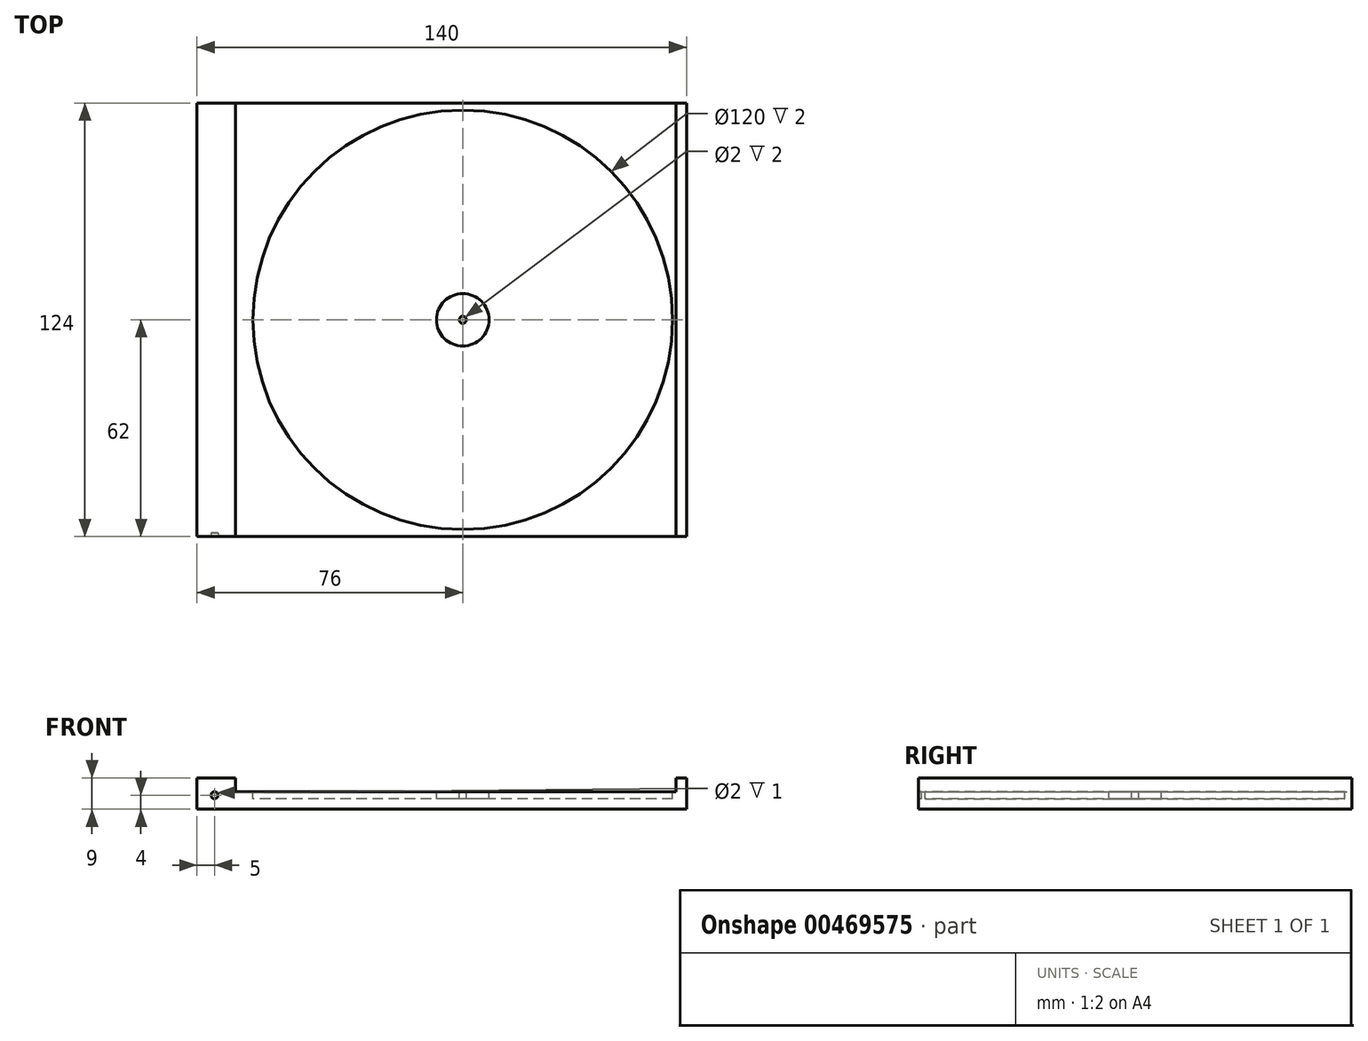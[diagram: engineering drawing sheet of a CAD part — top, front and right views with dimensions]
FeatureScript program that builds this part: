
annotation { "Feature Type Name" : "Feature", "Feature Type Description" : "" }
export const myFeature = defineFeature(function(context is Context, id is Id, definition is map)
    precondition{}
    {
        {
            var Q0;
            Q0=qCreatedBy(makeId("Top.planeOp"),FACE);
            var sketch = newSketch(context, id + "F0", { "sketchPlane" : qUnion([Q0])});
            skLineSegment(sketch, "E0.bottom", {"start": v(-70, 62) * mm, "end": v(70, 62) * mm});
            skLineSegment(sketch, "E0.top", {"start": v(-70, -62) * mm, "end": v(70, -62) * mm});
            skLineSegment(sketch, "E0.left", {"start": v(-70, 62) * mm, "end": v(-70, -62) * mm});
            skLineSegment(sketch, "E0.right", {"start": v(70, 62) * mm, "end": v(70, -62) * mm});
            skPoint(sketch, "E0.middle", {"position": v(0, 0) * mm});
            skLineSegment(sketch, "E1.0", {"start": v(-59, 62) * mm, "end": v(-59, -62) * mm});
            skLineSegment(sketch, "E2.0", {"start": v(67, 62) * mm, "end": v(67, -62) * mm});
            skSolve(sketch);
        }
        {
            var Q0;
            {var subQ0=sQuery(id+"F0.wireOp",EDGE,"E1.0");Q0=makeQuery(id+"F0.imprint","IMPRINT",FACE,{"disambiguationData":[TD([[makeQuery(id+"F0.imprint","IMPRINT",EDGE,{"derivedFrom":subQ0}),1.0]])]});}
            var Q1;
            {var subQ0=sQuery(id+"F0.wireOp",EDGE,"E0.left");Q1=makeQuery(id+"F0.imprint","IMPRINT",FACE,{"disambiguationData":[TD([[makeQuery(id+"F0.imprint","IMPRINT",EDGE,{"derivedFrom":subQ0}),1.0]])]});}
            var Q2;
            {var subQ0=sQuery(id+"F0.wireOp",EDGE,"E0.right");Q2=makeQuery(id+"F0.imprint","IMPRINT",FACE,{"disambiguationData":[TD([[makeQuery(id+"F0.imprint","IMPRINT",EDGE,{"derivedFrom":subQ0}),-1.0]])]});}
            var Q3;
            {var subQ1=sQuery(id+"F0.wireOp",EDGE,"E0.top");var subQ6=sQuery(id+"F0.wireOp",EDGE,"E2.0");var subQ9=makeQuery(id+"F0.imprint","INTERSECT",VERTEX,{"derivedFrom":[subQ1,subQ6]});Q3=makeQuery(id+"F0.imprint","IMPRINT",FACE,{"disambiguationData":[TD([[makeQuery(id+"F0.imprint","IMPRINT",EDGE,{"disambiguationData":[TD([[subQ9,1.0]])],"derivedFrom":subQ1}),1.0]])]});}
            var Q4;
            {var subQ1=sQuery(id+"F0.wireOp",EDGE,"E2.0");var subQ5=sQuery(id+"F0.wireOp",EDGE,"E0.bottom");var subQ6=makeQuery(id+"F0.imprint","INTERSECT",VERTEX,{"derivedFrom":[subQ5,subQ1]});Q4=makeQuery(id+"F0.imprint","IMPRINT",FACE,{"disambiguationData":[TD([[makeQuery(id+"F0.imprint","IMPRINT",EDGE,{"disambiguationData":[TD([[subQ6,1.0]])],"derivedFrom":subQ5}),-1.0]])]});}
            var Q5;
            {var subQ0=sQuery(id+"F0.wireOp",EDGE,"Rkooz21P-u4ya-tTto-kZgw-ZRGbYe9tmOBm");var subQ1=sQuery(id+"F0.wireOp",EDGE,"19190594-fffc-4df3-a4e9-dd137d7a63a9.0");var subQ2=makeQuery(id+"F0.imprint","INTERSECT",VERTEX,{"disambiguationData":[OD(0.0)],"derivedFrom":[subQ1,subQ0]});Q5=makeQuery(id+"F0.imprint","IMPRINT",FACE,{"disambiguationData":[TD([[makeQuery(id+"F0.imprint","IMPRINT",EDGE,{"disambiguationData":[TD([[subQ2,-1.0]])],"derivedFrom":subQ1}),1.0]])]});}
            var Q6;
            {var subQ0=sQuery(id+"F0.wireOp",EDGE,"dc407556-7fdb-4795-8f81-9fb84eb019c9.0");var subQ1=sQuery(id+"F0.wireOp",EDGE,"19190594-fffc-4df3-a4e9-dd137d7a63a9.0");var subQ2=makeQuery(id+"F0.imprint","INTERSECT",VERTEX,{"derivedFrom":[subQ1,subQ0]});Q6=makeQuery(id+"F0.imprint","IMPRINT",FACE,{"disambiguationData":[TD([[makeQuery(id+"F0.imprint","IMPRINT",EDGE,{"disambiguationData":[TD([[subQ2,-1.0]])],"derivedFrom":subQ1}),1.0]])]});}
            var Q7;
            {var subQ0=sQuery(id+"F0.wireOp",EDGE,"dc407556-7fdb-4795-8f81-9fb84eb019c9.0");var subQ1=sQuery(id+"F0.wireOp",EDGE,"19190594-fffc-4df3-a4e9-dd137d7a63a9.0");var subQ2=makeQuery(id+"F0.imprint","INTERSECT",VERTEX,{"derivedFrom":[subQ1,subQ0]});Q7=makeQuery(id+"F0.imprint","IMPRINT",FACE,{"disambiguationData":[TD([[makeQuery(id+"F0.imprint","IMPRINT",EDGE,{"disambiguationData":[TD([[subQ2,-1.0]])],"derivedFrom":subQ1}),-1.0]])]});}
            var Q8;
            {var subQ0=sQuery(id+"F0.wireOp",EDGE,"Rkooz21P-u4ya-tTto-kZgw-ZRGbYe9tmOBm");var subQ1=sQuery(id+"F0.wireOp",EDGE,"19190594-fffc-4df3-a4e9-dd137d7a63a9.0");var subQ2=makeQuery(id+"F0.imprint","INTERSECT",VERTEX,{"disambiguationData":[OD(0.0)],"derivedFrom":[subQ1,subQ0]});Q8=makeQuery(id+"F0.imprint","IMPRINT",FACE,{"disambiguationData":[TD([[makeQuery(id+"F0.imprint","IMPRINT",EDGE,{"disambiguationData":[TD([[subQ2,-1.0]])],"derivedFrom":subQ1}),-1.0]])]});}
            extrude(context, id + "F1", {"entities" : qUnion([Q0, Q1, Q2, Q3, Q4, Q5, Q6, Q7, Q8]), "depth" : 5 * mm});
        }
        {
            var Q0;
            {var subQ0=sQuery(id+"F0.wireOp",EDGE,"E0.left");Q0=makeQuery(id+"F0.imprint","IMPRINT",FACE,{"disambiguationData":[TD([[makeQuery(id+"F0.imprint","IMPRINT",EDGE,{"derivedFrom":subQ0}),1.0]])]});}
            var Q1;
            {var subQ0=sQuery(id+"F0.wireOp",EDGE,"E0.right");Q1=makeQuery(id+"F0.imprint","IMPRINT",FACE,{"disambiguationData":[TD([[makeQuery(id+"F0.imprint","IMPRINT",EDGE,{"derivedFrom":subQ0}),-1.0]])]});}
            extrude(context, id + "F2", {"entities" : qUnion([Q0, Q1]), "operationType" : NewBodyOperationType.ADD, "depth" : 9 * mm});
        }
        {
            var Q0;
            Q0=makeQuery(id+"F1.opExtrude","CAP_FACE",FACE,{"disambiguationData":[OSD([sQuery(id+"F0.wireOp",EDGE,"E0.bottom"),sQuery(id+"F0.wireOp",EDGE,"E0.top"),sQuery(id+"F0.wireOp",EDGE,"E0.left"),sQuery(id+"F0.wireOp",EDGE,"E0.right")])],"isStart":false});
            var sketch = newSketch(context, id + "F3", { "sketchPlane" : qUnion([Q0])});
            skLineSegment(sketch, "E3.0", {"start": v(-70, 0) * mm, "end": v(70, 0) * mm, "construction": true});
            skLineSegment(sketch, "E4.0", {"start": v(6, 62) * mm, "end": v(6, -62) * mm, "construction": true});
            skCircle(sketch, "E5", {"center": v(6, 0) * mm, "radius": 60 * mm});
            skCircle(sketch, "E6", {"center": v(6, 0) * mm, "radius": 7.5 * mm});
            skSolve(sketch);
        }
        {
            var Q0;
            Q0=makeQuery(id+"F3.imprint","IMPRINT",FACE,{"disambiguationData":[TD([[makeQuery(id+"F3.imprint","IMPRINT",EDGE,{"derivedFrom":sQuery(id+"F3.wireOp",EDGE,"E5")}),1.0]])]});
            var Q1;
            Q1=sQuery(id+"F3.wireOp",EDGE,"E5");
            extrude(context, id + "F4", {"entities" : qUnion([Q0]), "operationType" : NewBodyOperationType.REMOVE, "surfaceEntities" : qUnion([Q1]), "oppositeDirection" : true, "depth" : 2 * mm});
        }
        {
            var Q0;
            Q0=makeQuery(id+"F4.boolean.opBoolean","SPLIT",FACE,{"disambiguationData":[TD([makeQuery(id+"F4.opExtrude","SWEPT_FACE",FACE,{"disambiguationData":[OSD([sQuery(id+"F3.wireOp",EDGE,"E6")])]})])],"derivedFrom":makeQuery(id+"F1.opExtrude","CAP_FACE",FACE,{"disambiguationData":[OSD([sQuery(id+"F0.wireOp",EDGE,"E0.bottom"),sQuery(id+"F0.wireOp",EDGE,"E0.top"),sQuery(id+"F0.wireOp",EDGE,"E0.left"),sQuery(id+"F0.wireOp",EDGE,"E0.right")])],"isStart":false})});
            var sketch = newSketch(context, id + "F5", { "sketchPlane" : qUnion([Q0])});
            skCircle(sketch, "E7", {"center": v(6, 0) * mm, "radius": 1 * mm});
            skSolve(sketch);
        }
        {
            var Q0;
            Q0=makeQuery(id+"F5.imprint","IMPRINT",FACE,{"disambiguationData":[TD([[makeQuery(id+"F5.imprint","IMPRINT",EDGE,{"derivedFrom":sQuery(id+"F5.wireOp",EDGE,"E7")}),1.0]])]});
            extrude(context, id + "F6", {"entities" : qUnion([Q0]), "operationType" : NewBodyOperationType.REMOVE, "oppositeDirection" : true, "depth" : 2 * mm});
        }
        {
            var Q0;
            {var subQ0=sQuery(id+"F0.wireOp",EDGE,"E0.top");Q0=makeQuery(id+"F2.boolean.opBoolean","MERGE",FACE,{"derivedFrom":[makeQuery(id+"F1.opExtrude","SWEPT_FACE",FACE,{"disambiguationData":[OSD([subQ0])]}),makeQuery(id+"F2.opExtrude","SWEPT_FACE",FACE,{"disambiguationData":[OSD([subQ0]),TDD([makeQuery(id+"F0.imprint","IMPRINT",EDGE,{"disambiguationData":[TD([[makeQuery(id+"F0.imprint","INTERSECT",VERTEX,{"derivedFrom":[subQ0,sQuery(id+"F0.wireOp",EDGE,"E0.left")]}),-1.0]])],"derivedFrom":subQ0})])]}),makeQuery(id+"F2.opExtrude","SWEPT_FACE",FACE,{"disambiguationData":[OSD([subQ0]),TDD([makeQuery(id+"F0.imprint","IMPRINT",EDGE,{"disambiguationData":[TD([[makeQuery(id+"F0.imprint","INTERSECT",VERTEX,{"derivedFrom":[subQ0,sQuery(id+"F0.wireOp",EDGE,"E0.right")]}),1.0]])],"derivedFrom":subQ0})])]})]});}
            var sketch = newSketch(context, id + "F7", { "sketchPlane" : qUnion([Q0])});
            skLineSegment(sketch, "E8.0", {"start": v(-70, 4) * mm, "end": v(-59, 4) * mm, "construction": true});
            skLineSegment(sketch, "E9.0", {"start": v(-65, 9) * mm, "end": v(-65, 0) * mm, "construction": true});
            skCircle(sketch, "E10", {"center": v(-65, 4) * mm, "radius": 1 * mm});
            skSolve(sketch);
        }
        {
            var Q0;
            Q0=makeQuery(id+"F7.imprint","IMPRINT",FACE,{"disambiguationData":[TD([[makeQuery(id+"F7.imprint","IMPRINT",EDGE,{"derivedFrom":sQuery(id+"F7.wireOp",EDGE,"E10")}),1.0]])]});
            var Q1;
            Q1=sQuery(id+"F7.wireOp",EDGE,"E10");
            extrude(context, id + "F8", {"entities" : qUnion([Q0]), "operationType" : NewBodyOperationType.REMOVE, "surfaceEntities" : qUnion([Q1]), "oppositeDirection" : true, "depth" : 1 * mm});
        }
    });
